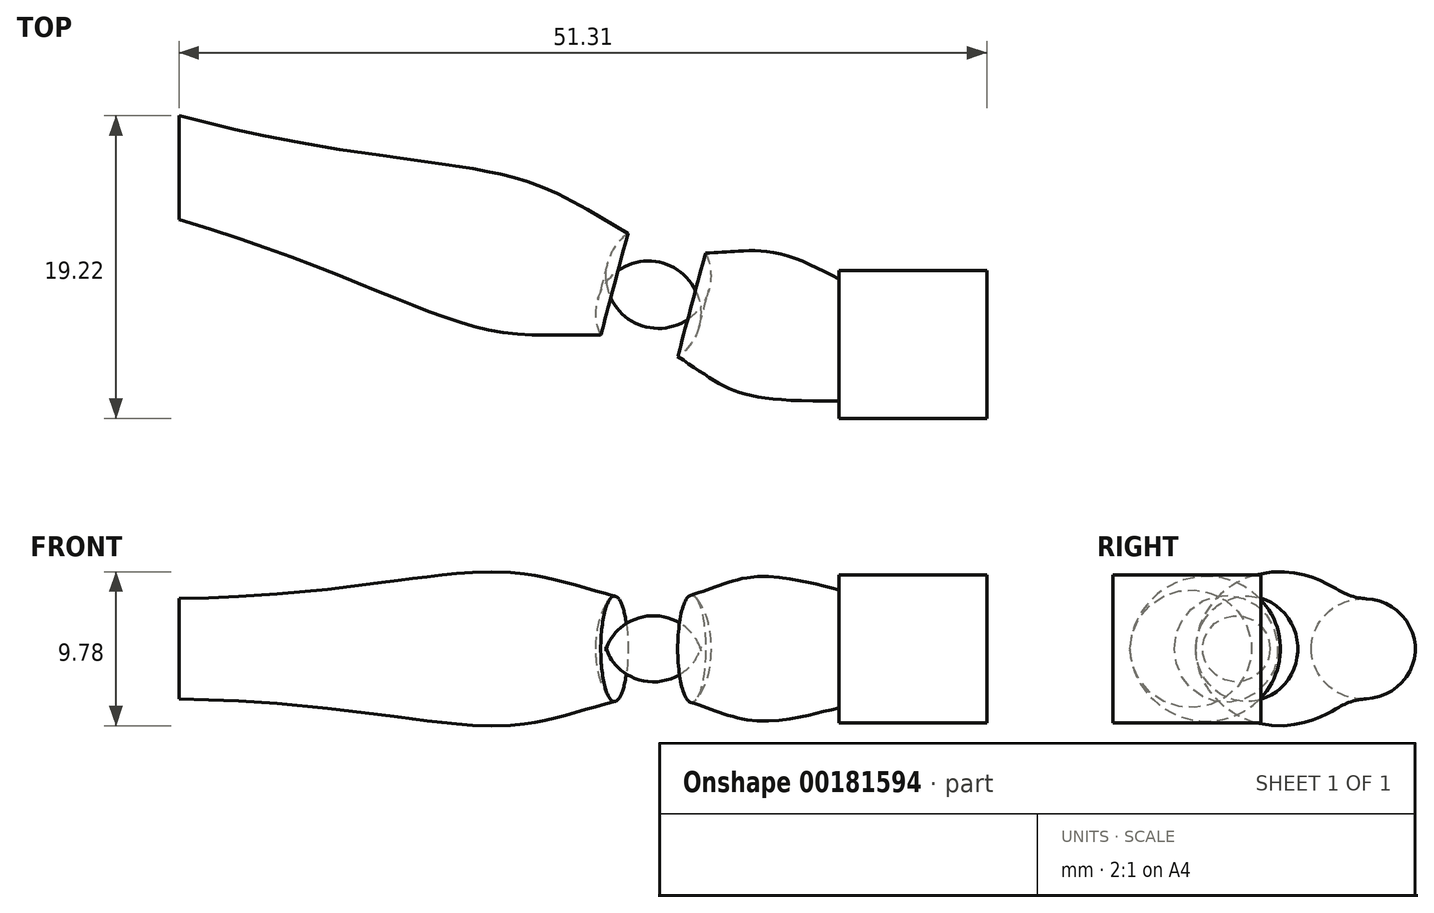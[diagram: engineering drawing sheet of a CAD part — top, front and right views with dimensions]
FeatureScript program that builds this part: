
annotation { "Feature Type Name" : "Feature", "Feature Type Description" : "" }
export const myFeature = defineFeature(function(context is Context, id is Id, definition is map)
    precondition{}
    {
        {
            var Q0;
            Q0=qCreatedBy(makeId("Top.planeOp"),FACE);
            var sketch = newSketch(context, id + "F0", { "sketchPlane" : qUnion([Q0])});
            skLineSegment(sketch, "E0.bottom", {"start": v(0, 0) * mm, "end": v(9.4, 0) * mm});
            skLineSegment(sketch, "E0.top", {"start": v(0, 9.4) * mm, "end": v(9.4, 9.4) * mm});
            skLineSegment(sketch, "E0.left", {"start": v(0, 0) * mm, "end": v(0, 9.4) * mm});
            skLineSegment(sketch, "E0.right", {"start": v(9.4, 0) * mm, "end": v(9.4, 9.4) * mm});
            skSolve(sketch);
        }
        {
            var Q0;
            Q0 = qSketchRegion(id + "F0", true);
            extrude(context, id + "F1", {"entities" : qUnion([Q0]), "endBound" : BoundingType.SYMMETRIC, "depth" : 9.4 * mm});
        }
        {
            var Q0;
            Q0=qCreatedBy(makeId("Top.planeOp"),FACE);
            var sketch = newSketch(context, id + "F2", { "sketchPlane" : qUnion([Q0])});
            skLineSegment(sketch, "E1", {"start": v(0, 4.7) * mm, "end": v(-46.58, 17.18) * mm, "construction": true});
            skLineSegment(sketch, "E2", {"start": v(-42.94, 16.2) * mm, "end": v(-43.76, 13.14) * mm});
            skFitSpline(sketch, "E3", {"points": [v(-43.76, 13.14) * mm, v(-21.28, 5.46) * mm, v(-12.6, 4.97) * mm, v(-7.87, 2.37) * mm, v(1.3, 1.11) * mm], "startDerivative": vector(99.92, -27.4) * mm, "endDerivative": vector(75.32, 1.26) * mm});
            skLineSegment(sketch, "E4", {"start": v(1.3, 1.11) * mm, "end": v(2.1, 4.13) * mm});
            skArc(sketch, "E5", {"start": v(-15.12, 5.28) * mm, "mid": v(-12.99, 3.46) * mm, "end": v(-10.23, 3.91) * mm});
            skLineSegment(sketch, "E6", {"start": v(-42.94, 16.2) * mm, "end": v(2.1, 4.13) * mm});
            skSolve(sketch);
        }
        {
            var Q0;
            Q0 = qSketchRegion(id + "F2", true);
            var Q1;
            Q1=sQuery(id+"F2.wireOp",EDGE,"E6");
            revolve(context, id + "F3", {"operationType" : NewBodyOperationType.ADD, "entities" : qUnion([Q0]), "axis" : qUnion([Q1]), "revolveType" : RevolveType.FULL});
        }
        {
            var Q0;
            Q0=qCreatedBy(makeId("Right.planeOp"),FACE);
            cPlane(context, id + "F4", {"entities" : qUnion([Q0]), "cplaneType" : CPlaneType.OFFSET, "offset" : 41.9 * mm, "oppositeDirection" : true, "width" : 152.4 * mm, "height" : 152.4 * mm});
        }
        {
            var Q0;
            Q0=qCreatedBy(id+"F4.planeOp",FACE);
            var sketch = newSketch(context, id + "F5", { "sketchPlane" : qUnion([Q0])});
            skCircle(sketch, "E7", {"center": v(16.2, 0) * mm, "radius": 6.42 * mm});
            skSolve(sketch);
        }
        {
            var Q0;
            Q0 = qSketchRegion(id + "F5", true);
            extrude(context, id + "F6", {"entities" : qUnion([Q0]), "operationType" : NewBodyOperationType.REMOVE, "endBound" : BoundingType.THROUGH_ALL, "oppositeDirection" : true, "depth" : 25.4 * mm});
        }
    });
